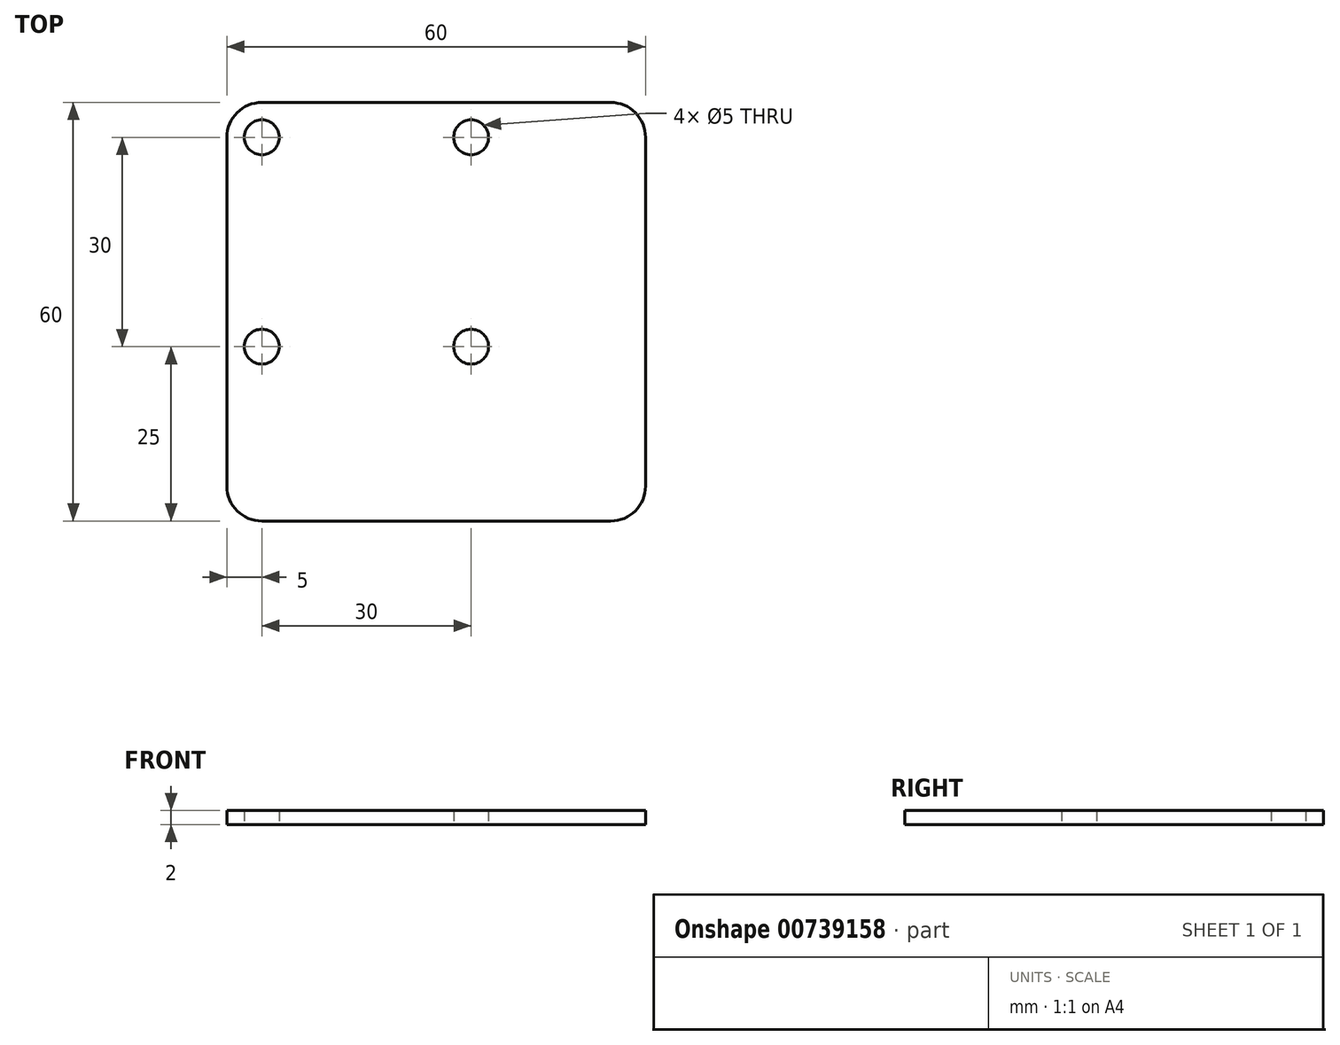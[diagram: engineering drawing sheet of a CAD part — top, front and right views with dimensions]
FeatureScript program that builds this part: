
annotation { "Feature Type Name" : "Feature", "Feature Type Description" : "" }
export const myFeature = defineFeature(function(context is Context, id is Id, definition is map)
    precondition{}
    {
        {
            var Q0;
            Q0=qCreatedBy(makeId("Top.planeOp"),FACE);
            var sketch = newSketch(context, id + "F0", { "sketchPlane" : qUnion([Q0])});
            skLineSegment(sketch, "E0.top", {"start": v(35, 20) * mm, "end": v(-15, 20) * mm});
            skLineSegment(sketch, "E0.right", {"start": v(-20, -35) * mm, "end": v(-20, 15) * mm});
            skPoint(sketch, "E0.middle", {"position": v(0, 0) * mm});
            skCircle(sketch, "E1", {"center": v(-15, -15) * mm, "radius": 2.5 * mm});
            skCircle(sketch, "E2", {"center": v(-15, 15) * mm, "radius": 2.5 * mm});
            skCircle(sketch, "E3", {"center": v(15, -15) * mm, "radius": 2.5 * mm});
            skCircle(sketch, "E4", {"center": v(15, 15) * mm, "radius": 2.5 * mm});
            skPoint(sketch, "E5.visualSharp", {"position": v(-20, 20) * mm});
            skArc(sketch, "E5.filletArc", {"start": v(-15, 20) * mm, "mid": v(-18.54, 18.54) * mm, "end": v(-20, 15) * mm});
            skPoint(sketch, "E6.visualSharp", {"position": v(20, 20) * mm});
            skPoint(sketch, "E7.visualSharp", {"position": v(20, -20) * mm});
            skPoint(sketch, "E8.visualSharp", {"position": v(-20, -20) * mm});
            skLineSegment(sketch, "E9.0", {"start": v(40, -35) * mm, "end": v(40, 15) * mm});
            skLineSegment(sketch, "E10.0", {"start": v(35, -40) * mm, "end": v(-15, -40) * mm});
            skPoint(sketch, "E11.visualSharp", {"position": v(40, 20) * mm});
            skArc(sketch, "E11.filletArc", {"start": v(40, 15) * mm, "mid": v(38.54, 18.54) * mm, "end": v(35, 20) * mm});
            skPoint(sketch, "E12.visualSharp", {"position": v(40, -40) * mm});
            skArc(sketch, "E12.filletArc", {"start": v(35, -40) * mm, "mid": v(38.54, -38.54) * mm, "end": v(40, -35) * mm});
            skPoint(sketch, "E13.visualSharp", {"position": v(-20, -40) * mm});
            skArc(sketch, "E13.filletArc", {"start": v(-20, -35) * mm, "mid": v(-18.54, -38.54) * mm, "end": v(-15, -40) * mm});
            skSolve(sketch);
        }
        {
            var Q0;
            Q0=makeQuery(id+"F0.imprint","IMPRINT",FACE,{"disambiguationData":[TD([[makeQuery(id+"F0.imprint","IMPRINT",EDGE,{"derivedFrom":sQuery(id+"F0.wireOp",EDGE,"E0.bottom")}),-1.0]])]});
            var Q1;
            Q1=makeQuery(id+"F0.imprint","IMPRINT",FACE,{"disambiguationData":[TD([[makeQuery(id+"F0.imprint","IMPRINT",EDGE,{"derivedFrom":sQuery(id+"F0.wireOp",EDGE,"E4")}),-1.0]])]});
            var Q2;
            Q2=makeQuery(id+"F0.imprint","IMPRINT",FACE,{"disambiguationData":[TD([[makeQuery(id+"F0.imprint","IMPRINT",EDGE,{"derivedFrom":sQuery(id+"F0.wireOp",EDGE,"E2")}),-1.0]])]});
            var Q3;
            Q3=makeQuery(id+"F0.imprint","IMPRINT",FACE,{"disambiguationData":[TD([[makeQuery(id+"F0.imprint","IMPRINT",EDGE,{"derivedFrom":sQuery(id+"F0.wireOp",EDGE,"E1")}),-1.0]])]});
            var Q4;
            Q4=makeQuery(id+"F0.imprint","IMPRINT",FACE,{"disambiguationData":[TD([[makeQuery(id+"F0.imprint","IMPRINT",EDGE,{"derivedFrom":sQuery(id+"F0.wireOp",EDGE,"E3")}),-1.0]])]});
            extrude(context, id + "F1", {"entities" : qUnion([Q0, Q1, Q2, Q3, Q4]), "depth" : 2 * mm, "offsetDistance" : 25 * mm});
        }
    });
